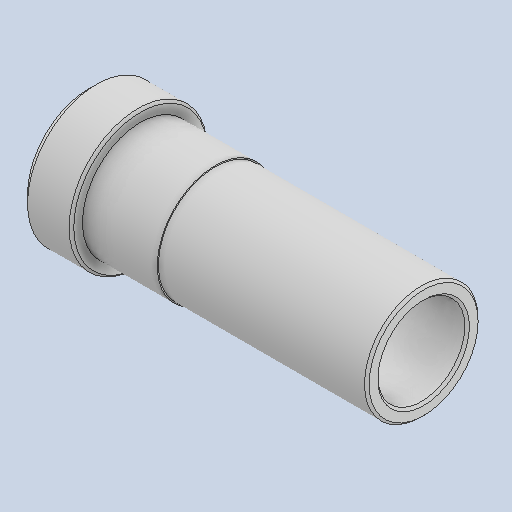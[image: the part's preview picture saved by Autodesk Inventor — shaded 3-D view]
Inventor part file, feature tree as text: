
AUTODESK INVENTOR PART (.ipt)
format: ipt  version: 2022.3 (Build 263350000, 350)  size: 133,632 bytes
history: native  units: in
note: dims shown in document units (in); Inventor stores cm internally (conversion verified against a paired STEP export)
features: chamfer x1
ambient origin geometry x8: Origin, YZ Plane, XZ Plane, XY Plane, X Axis, Y Axis, Z Axis, Center Point
bodies: Solid1 (feature_tree)
feature tree (1):
  chamfer  "Chamfer3"  [1 undecoded]
note: 1 required parameter value undecoded (feature->parameter linkage not recoverable at this tier; creation-order binding heuristic only, values carry confidence <= 0.55)
